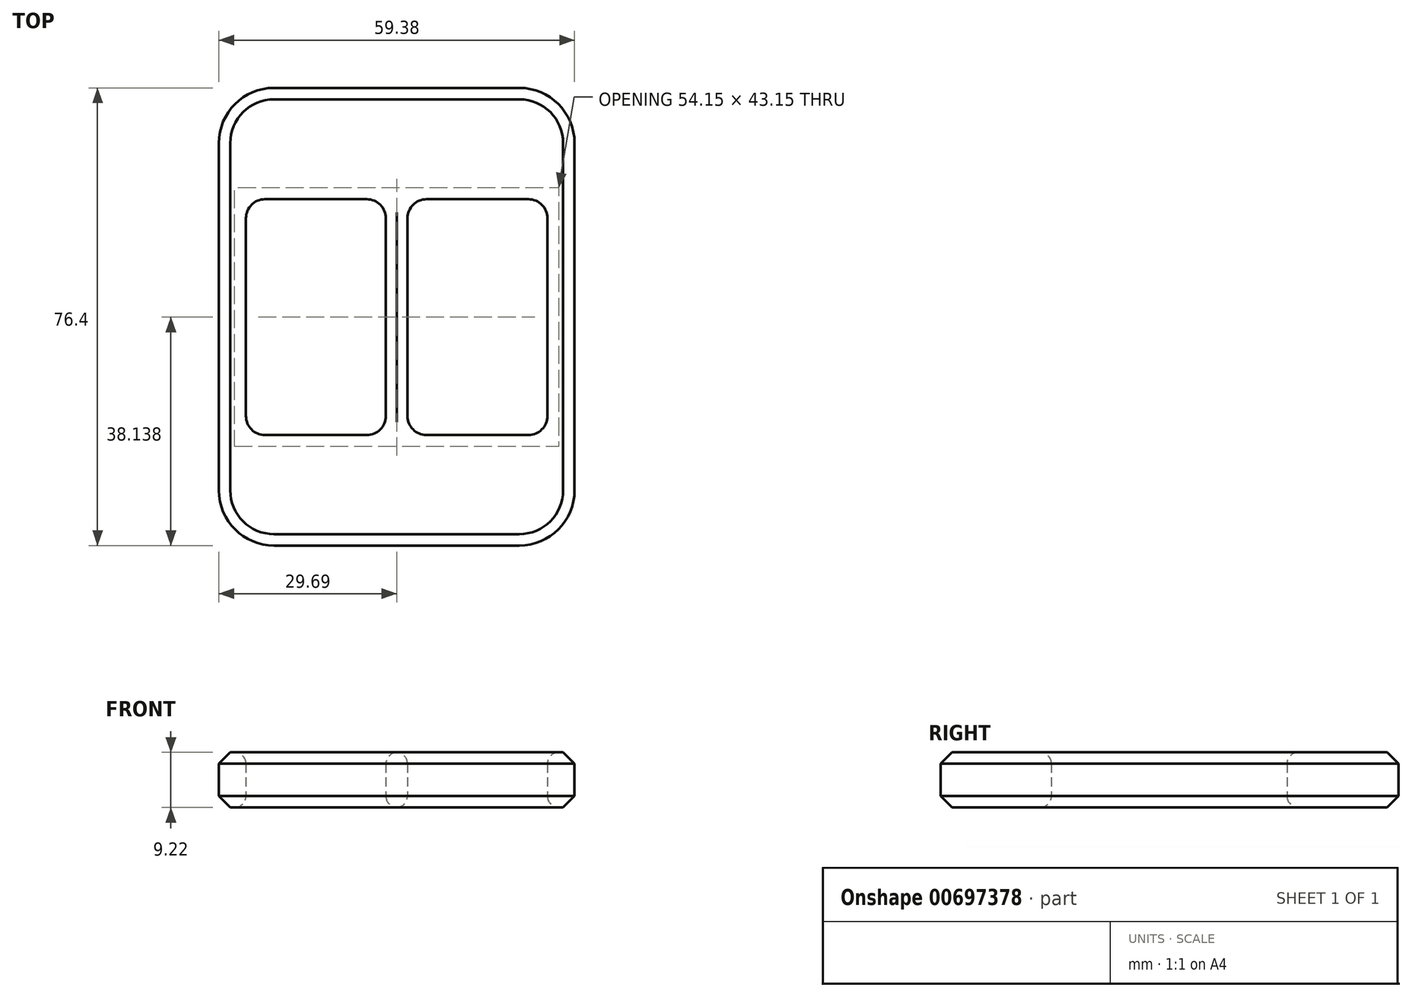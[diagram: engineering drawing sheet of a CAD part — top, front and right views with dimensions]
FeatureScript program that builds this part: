
annotation { "Feature Type Name" : "Feature", "Feature Type Description" : "" }
export const myFeature = defineFeature(function(context is Context, id is Id, definition is map)
    precondition{}
    {
        {
            var Q0;
            Q0=qCreatedBy(makeId("Top.planeOp"),FACE);
            var sketch = newSketch(context, id + "F0", { "sketchPlane" : qUnion([Q0])});
            skLineSegment(sketch, "E0.bottom", {"start": v(-20.47, 76.4) * mm, "end": v(20.47, 76.4) * mm});
            skLineSegment(sketch, "E0.top", {"start": v(-20.47, 0) * mm, "end": v(20.47, 0) * mm});
            skLineSegment(sketch, "E0.left", {"start": v(-29.7, 67.18) * mm, "end": v(-29.7, 9.22) * mm});
            skLineSegment(sketch, "E0.right", {"start": v(29.7, 67.18) * mm, "end": v(29.7, 9.22) * mm});
            skLineSegment(sketch, "E1", {"start": v(-25.17, 54.64) * mm, "end": v(-25.17, 21.64) * mm});
            skLineSegment(sketch, "E2", {"start": v(-22, 18.47) * mm, "end": v(-4.98, 18.47) * mm});
            skLineSegment(sketch, "E3", {"start": v(-1.8, 21.64) * mm, "end": v(-1.8, 54.64) * mm});
            skLineSegment(sketch, "E4", {"start": v(-4.98, 57.81) * mm, "end": v(-22, 57.81) * mm});
            skLineSegment(sketch, "E5", {"start": v(1.8, 54.64) * mm, "end": v(1.8, 21.64) * mm});
            skLineSegment(sketch, "E6", {"start": v(4.98, 18.47) * mm, "end": v(22, 18.47) * mm});
            skLineSegment(sketch, "E7", {"start": v(25.17, 21.64) * mm, "end": v(25.17, 54.64) * mm});
            skLineSegment(sketch, "E8", {"start": v(22, 57.81) * mm, "end": v(4.98, 57.81) * mm});
            skLineSegment(sketch, "E9", {"start": v(-29.7, 76.4) * mm, "end": v(29.7, 0) * mm, "construction": true});
            skPoint(sketch, "E10.visualSharp", {"position": v(-29.7, 76.4) * mm});
            skArc(sketch, "E10.filletArc", {"start": v(-20.47, 76.4) * mm, "mid": v(-27, 73.7) * mm, "end": v(-29.7, 67.18) * mm});
            skPoint(sketch, "E11.visualSharp", {"position": v(29.7, 76.4) * mm});
            skArc(sketch, "E11.filletArc", {"start": v(29.7, 67.18) * mm, "mid": v(27, 73.7) * mm, "end": v(20.47, 76.4) * mm});
            skPoint(sketch, "E12.visualSharp", {"position": v(29.7, 0) * mm});
            skArc(sketch, "E12.filletArc", {"start": v(20.47, 0) * mm, "mid": v(27, 2.7) * mm, "end": v(29.7, 9.22) * mm});
            skPoint(sketch, "E13.visualSharp", {"position": v(-29.7, 0) * mm});
            skArc(sketch, "E13.filletArc", {"start": v(-29.7, 9.22) * mm, "mid": v(-27, 2.7) * mm, "end": v(-20.47, 0) * mm});
            skLineSegment(sketch, "E14", {"start": v(-1.8, 57.81) * mm, "end": v(1.8, 57.81) * mm, "construction": true});
            skLineSegment(sketch, "E15", {"start": v(0, 0) * mm, "end": v(0, 88.7) * mm, "construction": true});
            skPoint(sketch, "E16", {"position": v(0, 57.81) * mm});
            skLineSegment(sketch, "E17", {"start": v(25.17, 57.81) * mm, "end": v(1.8, 18.47) * mm, "construction": true});
            skPoint(sketch, "E18.visualSharp", {"position": v(25.17, 57.81) * mm});
            skArc(sketch, "E18.filletArc", {"start": v(25.17, 54.64) * mm, "mid": v(24.24, 56.88) * mm, "end": v(22, 57.81) * mm});
            skPoint(sketch, "E19.visualSharp", {"position": v(1.8, 57.81) * mm});
            skArc(sketch, "E19.filletArc", {"start": v(4.98, 57.81) * mm, "mid": v(2.73, 56.88) * mm, "end": v(1.8, 54.64) * mm});
            skPoint(sketch, "E20.visualSharp", {"position": v(1.8, 18.47) * mm});
            skArc(sketch, "E20.filletArc", {"start": v(1.8, 21.64) * mm, "mid": v(2.73, 19.4) * mm, "end": v(4.98, 18.47) * mm});
            skPoint(sketch, "E21.visualSharp", {"position": v(25.17, 18.47) * mm});
            skArc(sketch, "E21.filletArc", {"start": v(22, 18.47) * mm, "mid": v(24.24, 19.4) * mm, "end": v(25.17, 21.64) * mm});
            skPoint(sketch, "E22.visualSharp", {"position": v(-1.8, 18.47) * mm});
            skArc(sketch, "E22.filletArc", {"start": v(-4.98, 18.47) * mm, "mid": v(-2.73, 19.4) * mm, "end": v(-1.8, 21.64) * mm});
            skPoint(sketch, "E23.visualSharp", {"position": v(-25.17, 18.47) * mm});
            skArc(sketch, "E23.filletArc", {"start": v(-25.17, 21.64) * mm, "mid": v(-24.24, 19.4) * mm, "end": v(-22, 18.47) * mm});
            skPoint(sketch, "E24.visualSharp", {"position": v(-25.17, 57.81) * mm});
            skArc(sketch, "E24.filletArc", {"start": v(-22, 57.81) * mm, "mid": v(-24.24, 56.88) * mm, "end": v(-25.17, 54.64) * mm});
            skPoint(sketch, "E25.visualSharp", {"position": v(-1.8, 57.81) * mm});
            skArc(sketch, "E25.filletArc", {"start": v(-1.8, 54.64) * mm, "mid": v(-2.73, 56.88) * mm, "end": v(-4.98, 57.81) * mm});
            skPoint(sketch, "E26", {"position": v(2.73, 56.88) * mm});
            skPoint(sketch, "E27", {"position": v(24.24, 19.4) * mm});
            skSolve(sketch);
        }
        {
            var Q0;
            Q0 = qSketchRegion(id + "F0", true);
            extrude(context, id + "F1", {"entities" : qUnion([Q0]), "depth" : 9.22 * mm, "offsetDistance" : 25.4 * mm});
        }
        {
            var Q0;
            Q0=makeQuery(id+"F1.opExtrude","CAP_EDGE",EDGE,{"disambiguationData":[OSD([sQuery(id+"F0.wireOp",EDGE,"E7")])],"isStart":true});
            var Q1;
            Q1=makeQuery(id+"F1.opExtrude","CAP_EDGE",EDGE,{"disambiguationData":[OSD([sQuery(id+"F0.wireOp",EDGE,"E1")])],"isStart":true});
            var Q2;
            Q2=makeQuery(id+"F1.opExtrude","CAP_EDGE",EDGE,{"disambiguationData":[OSD([sQuery(id+"F0.wireOp",EDGE,"E3")])],"isStart":false});
            var Q3;
            Q3=makeQuery(id+"F1.opExtrude","CAP_EDGE",EDGE,{"disambiguationData":[OSD([sQuery(id+"F0.wireOp",EDGE,"E8")])],"isStart":false});
            fillet(context, id + "F2", {"entities" : qUnion([Q0, Q1, Q2, Q3]), "radius" : 1.9 * mm, "tangentPropagation" : true, "allowEdgeOverflow" : false});
        }
        {
            var Q0;
            Q0=makeQuery(id+"F1.opExtrude","CAP_EDGE",EDGE,{"disambiguationData":[OSD([sQuery(id+"F0.wireOp",EDGE,"E0.left")])],"isStart":false});
            var Q1;
            Q1=makeQuery(id+"F1.opExtrude","CAP_EDGE",EDGE,{"disambiguationData":[OSD([sQuery(id+"F0.wireOp",EDGE,"E0.left")])],"isStart":true});
            chamfer(context, id + "F3", {"entities" : qUnion([Q0, Q1]), "width" : 1.9 * mm, "tangentPropagation" : true});
        }
    });
